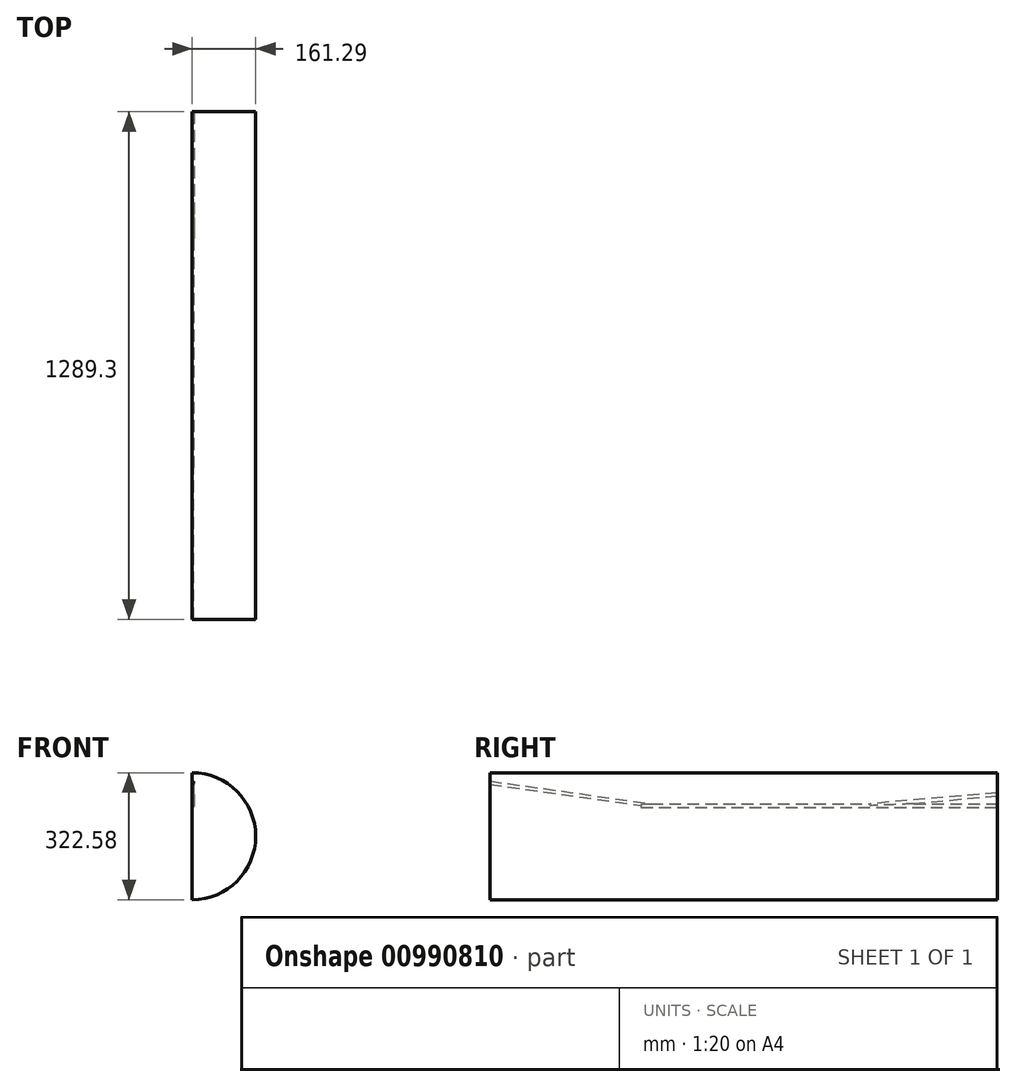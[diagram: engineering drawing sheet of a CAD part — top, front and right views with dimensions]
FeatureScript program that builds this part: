
annotation { "Feature Type Name" : "Feature", "Feature Type Description" : "" }
export const myFeature = defineFeature(function(context is Context, id is Id, definition is map)
    precondition{}
    {
        {
            var Q0;
            Q0=qCreatedBy(makeId("Front.planeOp"),FACE);
            var sketch = newSketch(context, id + "F0", { "sketchPlane" : qUnion([Q0])});
            skCircle(sketch, "E0", {"center": v(0, 0) * mm, "radius": 161.3 * mm});
            skSolve(sketch);
        }
        {
            var Q0;
            Q0=makeQuery(id+"F0.imprint","IMPRINT",FACE,{"disambiguationData":[TD([[makeQuery(id+"F0.imprint","IMPRINT",EDGE,{"derivedFrom":sQuery(id+"F0.wireOp",EDGE,"E0")}),1.0]])]});
            extrude(context, id + "F1", {"entities" : qUnion([Q0]), "depth" : 1289.3 * mm, "offsetDistance" : 25.4 * mm});
        }
        {
            var Q0;
            Q0=makeQuery(id+"F1.opExtrude","CAP_FACE",FACE,{"disambiguationData":[OSD([sQuery(id+"F0.wireOp",EDGE,"E0")])],"isStart":true});
            var sketch = newSketch(context, id + "F2", { "sketchPlane" : qUnion([Q0])});
            skPoint(sketch, "E1", {"position": v(0, 77.72) * mm});
            skCircle(sketch, "E2", {"center": v(0, 77.72) * mm, "radius": 4.83 * mm});
            skSolve(sketch);
        }
        {
            var Q0;
            Q0 = qSketchRegion(id + "F2", true);
            extrude(context, id + "F3", {"entities" : qUnion([Q0]), "operationType" : NewBodyOperationType.REMOVE, "oppositeDirection" : true, "depth" : 905 * mm, "offsetDistance" : 25.4 * mm});
        }
        {
            var Q0;
            Q0=qCreatedBy(makeId("Right.planeOp"),FACE);
            var sketch = newSketch(context, id + "F4", { "sketchPlane" : qUnion([Q0])});
            skPoint(sketch, "E3", {"position": v(-1289.3, 136.27) * mm});
            skLineSegment(sketch, "E4", {"start": v(0, 0) * mm, "end": v(-1377.67, 0) * mm});
            skLineSegment(sketch, "E5", {"start": v(-1289.3, 136.27) * mm, "end": v(-879.31, 78.65) * mm});
            skLineSegment(sketch, "E6.0", {"start": v(-1288.76, 140.17) * mm, "end": v(-879.31, 82.63) * mm});
            skLineSegment(sketch, "E7", {"start": v(-879.31, 78.65) * mm, "end": v(-879.31, 82.63) * mm});
            skLineSegment(sketch, "E8", {"start": v(-1288.76, 140.17) * mm, "end": v(-1291.59, 140.57) * mm});
            skLineSegment(sketch, "E9", {"start": v(-1291.59, 140.57) * mm, "end": v(-1289.3, 136.27) * mm});
            skSolve(sketch);
        }
        {
            var Q0;
            Q0 = qSketchRegion(id + "F4", true);
            var Q1;
            Q1=sQuery(id+"F4.wireOp",EDGE,"E5");
            revolve(context, id + "F5", {"operationType" : NewBodyOperationType.REMOVE, "surfaceOperationType" : NewSurfaceOperationType.NEW, "entities" : qUnion([Q0]), "axis" : qUnion([Q1]), "revolveType" : RevolveType.FULL, "oppositeDirection" : true});
        }
        {
            var Q0;
            Q0=qCreatedBy(makeId("Right.planeOp"),FACE);
            var sketch = newSketch(context, id + "F6", { "sketchPlane" : qUnion([Q0])});
            skPoint(sketch, "E10", {"position": v(0, 105.9) * mm});
            skLineSegment(sketch, "E11", {"start": v(36.26, 109.08) * mm, "end": v(-321.6, 77.77) * mm});
            skLineSegment(sketch, "E12.0", {"start": v(36.68, 104.27) * mm, "end": v(-321.18, 72.96) * mm});
            skLineSegment(sketch, "E13", {"start": v(36.26, 109.08) * mm, "end": v(36.68, 104.27) * mm});
            skLineSegment(sketch, "E14", {"start": v(-321.18, 72.96) * mm, "end": v(-321.6, 77.77) * mm});
            skSolve(sketch);
        }
        {
            var Q0;
            Q0=makeQuery(id+"F1.opExtrude","CAP_FACE",FACE,{"disambiguationData":[OSD([sQuery(id+"F0.wireOp",EDGE,"E0")])],"isStart":true});
            var sketch = newSketch(context, id + "F7", { "sketchPlane" : qUnion([Q0])});
            skLineSegment(sketch, "E15", {"start": v(0, 174.54) * mm, "end": v(0, -186.87) * mm});
            skLineSegment(sketch, "E16", {"start": v(0, -186.87) * mm, "end": v(195.72, -99.05) * mm});
            skLineSegment(sketch, "E17", {"start": v(195.72, -99.05) * mm, "end": v(195.72, 72.07) * mm});
            skLineSegment(sketch, "E18", {"start": v(195.72, 72.07) * mm, "end": v(88.4, 168.14) * mm});
            skLineSegment(sketch, "E19", {"start": v(88.4, 168.14) * mm, "end": v(0, 174.12) * mm});
            skSolve(sketch);
        }
        {
            var Q0;
            Q0 = qSketchRegion(id + "F7", true);
            extrude(context, id + "F8", {"entities" : qUnion([Q0]), "operationType" : NewBodyOperationType.REMOVE, "oppositeDirection" : true, "depth" : 1323.34 * mm, "offsetDistance" : 25.4 * mm});
        }
        {
            var Q0;
            Q0 = qSketchRegion(id + "F6", true);
            var Q1;
            Q1=sQuery(id+"F6.wireOp",EDGE,"E11");
            revolve(context, id + "F9", {"operationType" : NewBodyOperationType.REMOVE, "surfaceOperationType" : NewSurfaceOperationType.NEW, "entities" : qUnion([Q0]), "axis" : qUnion([Q1]), "revolveType" : RevolveType.FULL, "oppositeDirection" : true});
        }
    });
